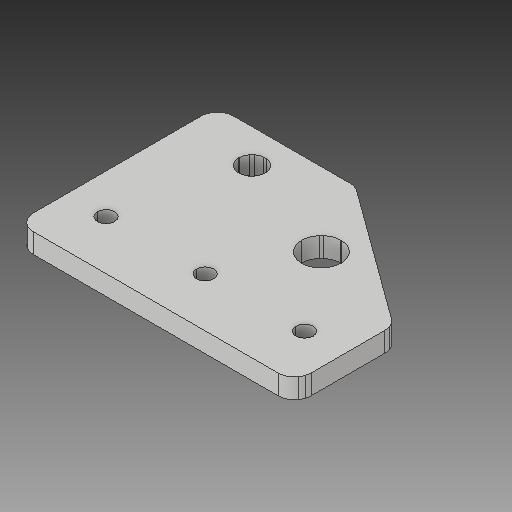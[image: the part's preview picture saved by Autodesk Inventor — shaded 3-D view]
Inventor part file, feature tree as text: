
AUTODESK INVENTOR PART (.ipt)
format: ipt  version: 2018 (Build 220112000, 112)  size: 272,384 bytes
history: native  units: mm
features: sketch x4, extrude x3, hole x1, projected_geometry x1
ambient origin geometry x8: Origin, YZ Plane, XZ Plane, XY Plane, X Axis, Y Axis, Z Axis, Center Point
bodies: Solid1 (feature_tree)
feature tree (9):
  extrude  "Extrusion1"  Depth=10.0mm TaperAngle=0.0deg
  hole  "Hole1"  [1 undecoded]
  extrude  "Extrusion2"  [1 undecoded]
  extrude  "Extrusion3"  [1 undecoded]
  sketch  "Sketch1"  dims[d0=6.0mm d1=0.0mm]
  sketch  "Sketch2"  dims[d2=5.2mm d3=6.0mm d4=4.0mm d5=2.0mm d6=90.0deg d7=8.0mm d8=20.594885mm d9=10.0mm d10=0.0mm]
  projected_geometry  "Projected Loop1"
  sketch  "Sketch3"  dims[d11=12.0mm d12=10.0mm d13=0.0mm]
  sketch  "Sketch5"
note: 3 required parameter values undecoded (feature->parameter linkage not recoverable at this tier; creation-order binding heuristic only, values carry confidence <= 0.55)
